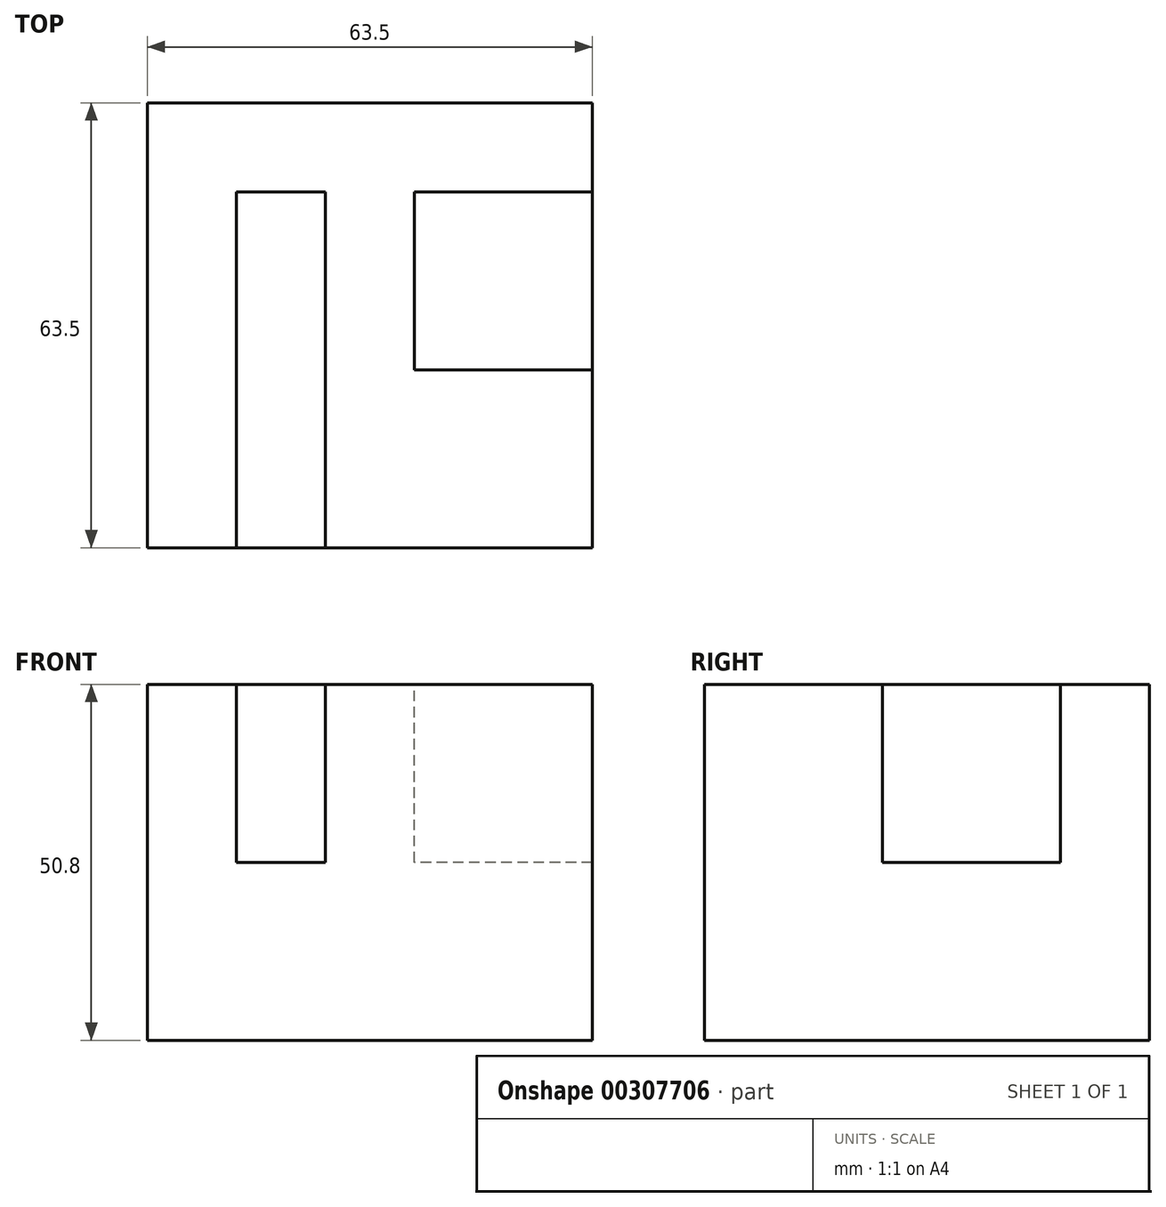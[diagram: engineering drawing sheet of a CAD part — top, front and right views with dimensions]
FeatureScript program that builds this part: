
annotation { "Feature Type Name" : "Feature", "Feature Type Description" : "" }
export const myFeature = defineFeature(function(context is Context, id is Id, definition is map)
    precondition{}
    {
        {
            var Q0;
            Q0=qCreatedBy(makeId("Top.planeOp"),FACE);
            var sketch = newSketch(context, id + "F0", { "sketchPlane" : qUnion([Q0])});
            skLineSegment(sketch, "E0.bottom", {"start": v(-34.9, 34.55) * mm, "end": v(28.6, 34.55) * mm});
            skLineSegment(sketch, "E0.top", {"start": v(-34.9, -28.95) * mm, "end": v(28.6, -28.95) * mm});
            skLineSegment(sketch, "E0.left", {"start": v(-34.9, 34.55) * mm, "end": v(-34.9, -28.95) * mm});
            skLineSegment(sketch, "E0.right", {"start": v(28.6, 34.55) * mm, "end": v(28.6, -28.95) * mm});
            skSolve(sketch);
        }
        {
            var Q0;
            Q0 = qSketchRegion(id + "F0", true);
            extrude(context, id + "F1", {"entities" : qUnion([Q0]), "depth" : 50.8 * mm});
        }
        {
            var Q0;
            Q0=makeQuery(id+"F1.opExtrude","CAP_FACE",FACE,{"disambiguationData":[OSD([sQuery(id+"F0.wireOp",EDGE,"E0.bottom"),sQuery(id+"F0.wireOp",EDGE,"E0.top"),sQuery(id+"F0.wireOp",EDGE,"E0.left"),sQuery(id+"F0.wireOp",EDGE,"E0.right")])],"isStart":false});
            var sketch = newSketch(context, id + "F2", { "sketchPlane" : qUnion([Q0])});
            skLineSegment(sketch, "E1.bottom", {"start": v(-9.5, -28.95) * mm, "end": v(-22.2, -28.95) * mm});
            skLineSegment(sketch, "E1.top", {"start": v(-9.5, 21.85) * mm, "end": v(-22.2, 21.85) * mm});
            skLineSegment(sketch, "E1.left", {"start": v(-9.5, -28.95) * mm, "end": v(-9.5, 21.85) * mm});
            skLineSegment(sketch, "E1.right", {"start": v(-22.2, -28.95) * mm, "end": v(-22.2, 21.85) * mm});
            skSolve(sketch);
        }
        {
            var Q0;
            Q0=makeQuery(id+"F2.imprint","IMPRINT",FACE,{"disambiguationData":[TD([[makeQuery(id+"F2.imprint","IMPRINT",EDGE,{"derivedFrom":sQuery(id+"F2.wireOp",EDGE,"E1.bottom")}),1.0]])]});
            extrude(context, id + "F3", {"entities" : qUnion([Q0]), "operationType" : NewBodyOperationType.REMOVE, "oppositeDirection" : true, "depth" : 25.4 * mm});
        }
        {
            var Q0;
            Q0=makeQuery(id+"F1.opExtrude","CAP_FACE",FACE,{"disambiguationData":[OSD([sQuery(id+"F0.wireOp",EDGE,"E0.bottom"),sQuery(id+"F0.wireOp",EDGE,"E0.top"),sQuery(id+"F0.wireOp",EDGE,"E0.left"),sQuery(id+"F0.wireOp",EDGE,"E0.right")])],"isStart":false});
            var sketch = newSketch(context, id + "F4", { "sketchPlane" : qUnion([Q0])});
            skLineSegment(sketch, "E2.bottom", {"start": v(28.6, 21.85) * mm, "end": v(3.2, 21.85) * mm});
            skLineSegment(sketch, "E2.top", {"start": v(28.6, -3.55) * mm, "end": v(3.2, -3.55) * mm});
            skLineSegment(sketch, "E2.left", {"start": v(28.6, 21.85) * mm, "end": v(28.6, -3.55) * mm});
            skLineSegment(sketch, "E2.right", {"start": v(3.2, 21.85) * mm, "end": v(3.2, -3.55) * mm});
            skSolve(sketch);
        }
        {
            var Q0;
            Q0 = qSketchRegion(id + "F4", true);
            extrude(context, id + "F5", {"entities" : qUnion([Q0]), "operationType" : NewBodyOperationType.REMOVE, "oppositeDirection" : true, "depth" : 25.4 * mm});
        }
    });
